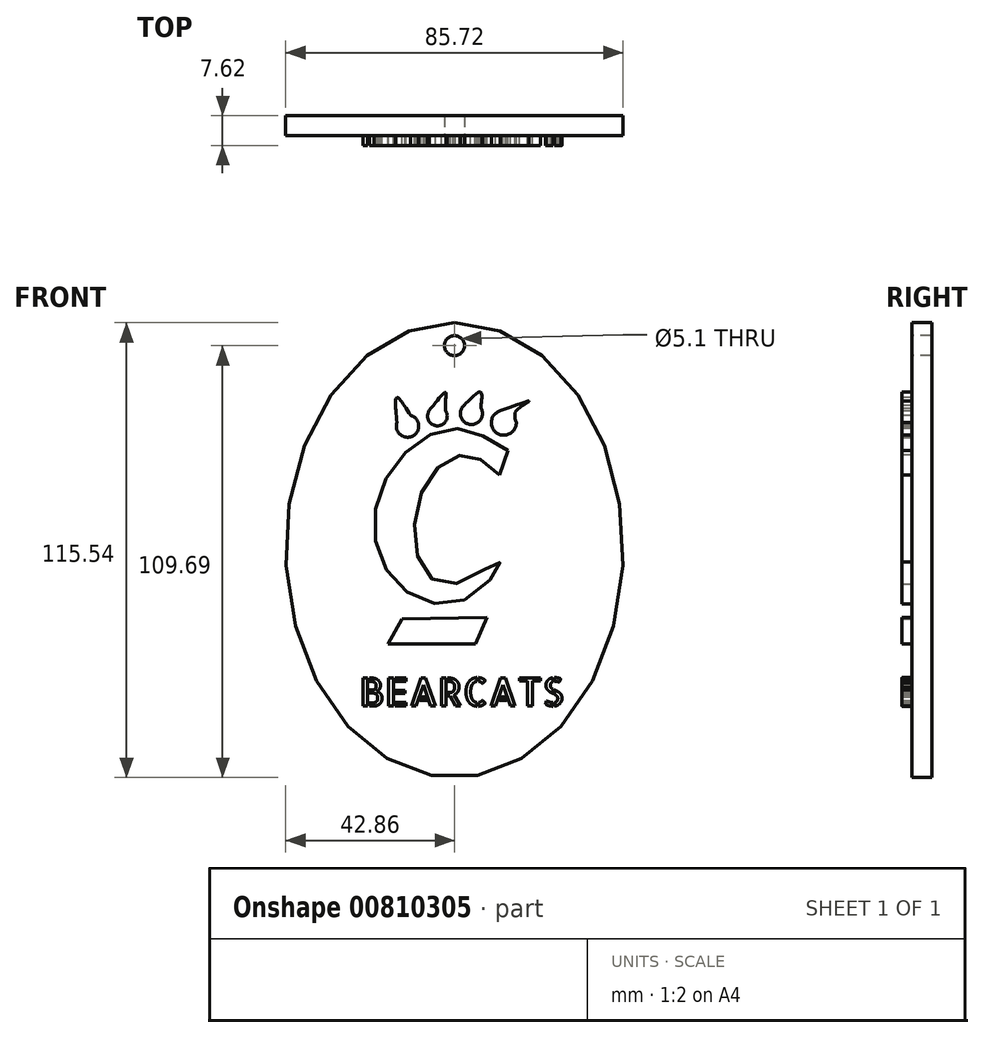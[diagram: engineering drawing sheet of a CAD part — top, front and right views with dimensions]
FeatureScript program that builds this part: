
annotation { "Feature Type Name" : "Feature", "Feature Type Description" : "" }
export const myFeature = defineFeature(function(context is Context, id is Id, definition is map)
    precondition{}
    {
        {
            var Q0;
            Q0=qCreatedBy(makeId("Front.planeOp"),FACE);
            var sketch = newSketch(context, id + "F0", { "sketchPlane" : qUnion([Q0])});
            skEllipse(sketch, "E0", {"center": v(0, 0) * mm, "majorRadius": 57.77 * mm, "minorRadius": 42.86 * mm, "majorAxis": v(0, 1)});
            skSolve(sketch);
        }
        {
            var Q0;
            Q0 = qSketchRegion(id + "F0", true);
            extrude(context, id + "F1", {"entities" : qUnion([Q0]), "depth" : 5.08 * mm, "offsetDistance" : 25.4 * mm});
        }
        {
            var Q0;
            Q0=makeQuery(id+"F1.opExtrude","CAP_FACE",FACE,{"disambiguationData":[OSD([sQuery(id+"F0.wireOp",EDGE,"E0")])],"isStart":false});
            var sketch = newSketch(context, id + "F2", { "sketchPlane" : qUnion([Q0])});
            skLineSegment(sketch, "E1", {"start": v(11.44, 19.11) * mm, "end": v(13.58, 25.25) * mm});
            skFitSpline(sketch, "E2", {"points": [v(11.44, 19.11) * mm, v(2.63, 24.18) * mm, v(-7.24, 16.98) * mm, v(-9.11, -2.24) * mm, v(0, -8.65) * mm, v(11.44, -3.04) * mm, v(4.5, -11.58) * mm, v(-11.51, -11.05) * mm, v(-20.32, 4.16) * mm, v(-14.45, 22.58) * mm, v(0, 30.86) * mm, v(13.58, 25.25) * mm], "startDerivative": vector(-110.76, 98.47) * mm, "endDerivative": vector(144.13, -93) * mm});
            skArc(sketch, "E3", {"start": v(11.7, 35.4) * mm, "mid": v(10.67, 29.77) * mm, "end": v(15.71, 32.46) * mm});
            skFitSpline(sketch, "E4", {"points": [v(15.71, 32.46) * mm, v(15.71, 35.4) * mm, v(18.91, 37.8) * mm, v(11.7, 35.4) * mm], "startDerivative": vector(-3.93, 11.2) * mm, "endDerivative": vector(-26.15, -9.48) * mm});
            skArc(sketch, "E5", {"start": v(2.53, 36.88) * mm, "mid": v(3.79, 31.94) * mm, "end": v(6.75, 36.09) * mm});
            skFitSpline(sketch, "E6", {"points": [v(6.75, 36.09) * mm, v(6.75, 36.88) * mm], "startDerivative": vector(0, 0.8) * mm, "endDerivative": vector(0, 0.8) * mm});
            skFitSpline(sketch, "E7", {"points": [v(6.75, 36.35) * mm, v(6.75, 36.88) * mm, v(6.75, 40.04) * mm, v(2.53, 36.88) * mm], "startDerivative": vector(-0.3, 2.17) * mm, "endDerivative": vector(-11.52, -11.8) * mm});
            skArc(sketch, "E8", {"start": v(-6.45, 35.4) * mm, "mid": v(-4.33, 31.54) * mm, "end": v(-2.22, 35.4) * mm});
            skFitSpline(sketch, "E9", {"points": [v(-2.22, 35.4) * mm, v(-2.22, 38.46) * mm, v(-2.22, 40.04) * mm, v(-6.45, 35.4) * mm], "startDerivative": vector(-0.47, 9.62) * mm, "endDerivative": vector(-12.5, -15.97) * mm});
            skArc(sketch, "E10", {"start": v(-14.63, 32.4) * mm, "mid": v(-10.57, 28.98) * mm, "end": v(-11.2, 34.24) * mm});
            skFitSpline(sketch, "E11", {"points": [v(-14.63, 32.4) * mm, v(-14.63, 38.72) * mm, v(-11.2, 34.24) * mm], "startDerivative": vector(-1.82, 17.86) * mm, "endDerivative": vector(8.78, -14.47) * mm});
            skLineSegment(sketch, "E12", {"start": v(-13.38, -17.45) * mm, "end": v(-16.85, -23.86) * mm});
            skLineSegment(sketch, "E13", {"start": v(-16.85, -23.86) * mm, "end": v(5.3, -23.86) * mm});
            skLineSegment(sketch, "E14", {"start": v(5.3, -23.86) * mm, "end": v(8.24, -17.19) * mm});
            skLineSegment(sketch, "E15", {"start": v(8.24, -17.19) * mm, "end": v(-13.38, -17.45) * mm});
            skSolve(sketch);
        }
        {
            var Q0;
            Q0 = qSketchRegion(id + "F2", true);
            extrude(context, id + "F3", {"entities" : qUnion([Q0]), "operationType" : NewBodyOperationType.ADD, "depth" : 2.54 * mm, "offsetDistance" : 25.4 * mm});
        }
        {
            var Q0;
            Q0=makeQuery(id+"F1.opExtrude","CAP_FACE",FACE,{"disambiguationData":[OSD([sQuery(id+"F0.wireOp",EDGE,"E0")])],"isStart":false});
            var sketch = newSketch(context, id + "F4", { "sketchPlane" : qUnion([Q0])});
            skText(sketch, "E16", { "text": "BEARCATS", "fontName": "AllertaStencil-Regular.ttf"});
            const initialGuessF4  = {"E16": [-0.02413, -0.03965, 1, 0, 0.00713]};
            skSetInitialGuess(sketch, initialGuessF4);
            skSolve(sketch);
        }
        {
            var Q0;
            Q0 = qSketchRegion(id + "F4", true);
            extrude(context, id + "F5", {"entities" : qUnion([Q0]), "operationType" : NewBodyOperationType.ADD, "depth" : 2.54 * mm, "offsetDistance" : 25.4 * mm});
        }
        {
            var Q0;
            Q0=makeQuery(id+"F1.opExtrude","CAP_FACE",FACE,{"disambiguationData":[OSD([sQuery(id+"F0.wireOp",EDGE,"E0")])],"isStart":false});
            var sketch = newSketch(context, id + "F6", { "sketchPlane" : qUnion([Q0])});
            skCircle(sketch, "E17", {"center": v(0, 51.92) * mm, "radius": 2.55 * mm});
            skSolve(sketch);
        }
        {
            var Q0;
            Q0 = qSketchRegion(id + "F6", true);
            extrude(context, id + "F7", {"entities" : qUnion([Q0]), "operationType" : NewBodyOperationType.REMOVE, "oppositeDirection" : true, "depth" : 5.08 * mm, "offsetDistance" : 25.4 * mm});
        }
    });
